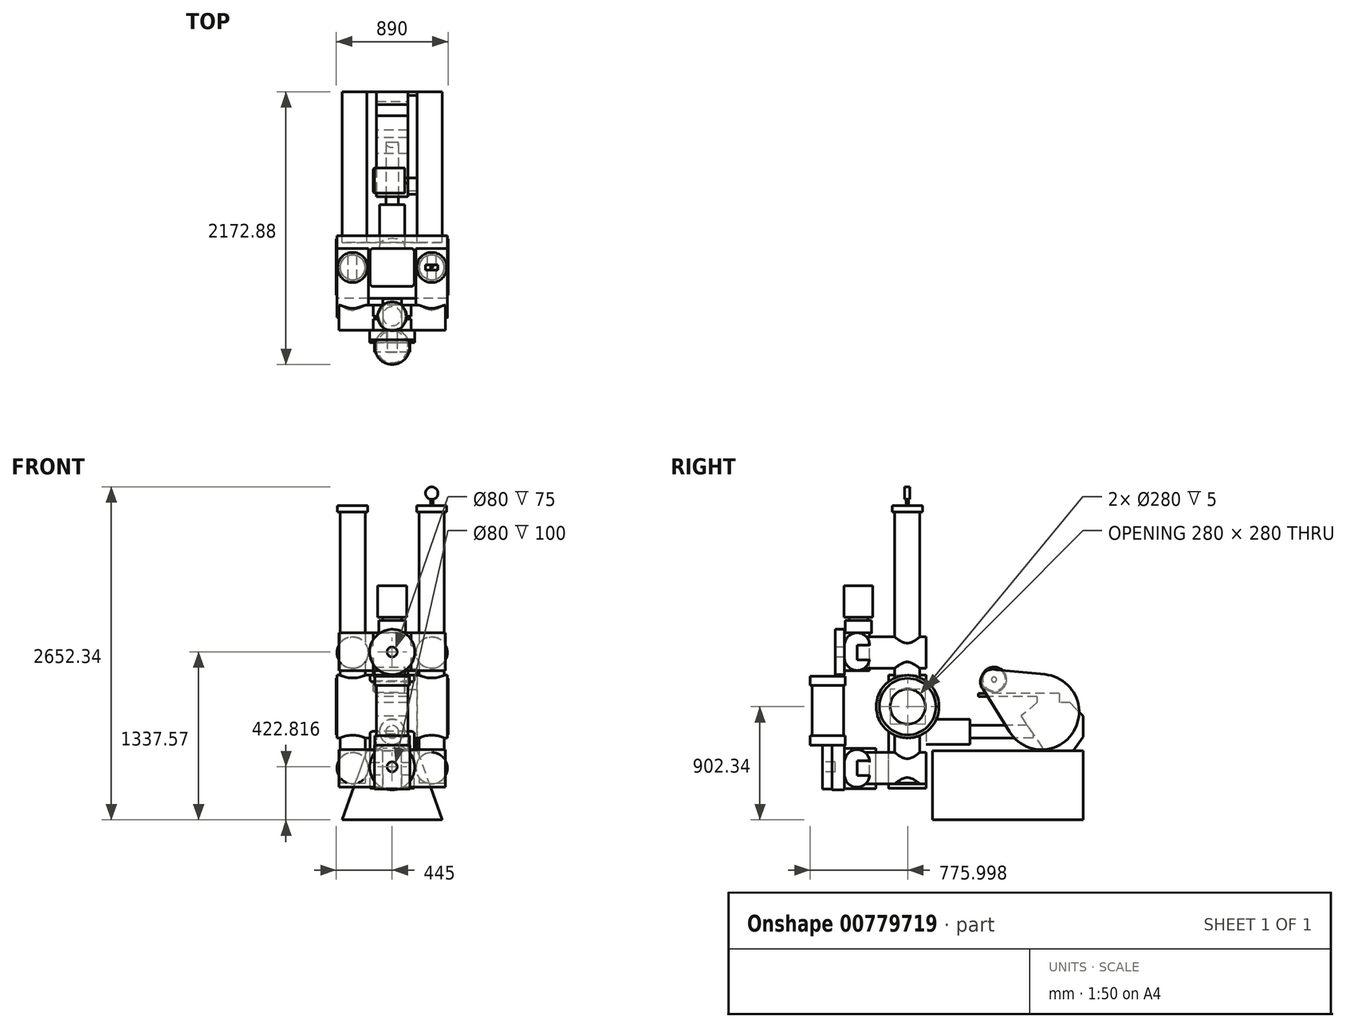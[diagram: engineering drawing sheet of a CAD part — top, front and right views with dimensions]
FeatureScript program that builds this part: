
annotation { "Feature Type Name" : "Feature", "Feature Type Description" : "" }
export const myFeature = defineFeature(function(context is Context, id is Id, definition is map)
    precondition{}
    {
        {
            var Q0;
            Q0=qCreatedBy(makeId("Front.planeOp"),FACE);
            var sketch = newSketch(context, id + "F0", { "sketchPlane" : qUnion([Q0])});
            skLineSegment(sketch, "E0", {"start": v(-400, 0) * mm, "end": v(-200, 550) * mm});
            skLineSegment(sketch, "E1", {"start": v(-200, 550) * mm, "end": v(200, 550) * mm});
            skLineSegment(sketch, "E2", {"start": v(200, 550) * mm, "end": v(400, 0) * mm});
            skLineSegment(sketch, "E3", {"start": v(400, 0) * mm, "end": v(-400, 0) * mm});
            skSolve(sketch);
        }
        {
            var Q0;
            Q0=makeQuery(id+"F0.imprint","IMPRINT",FACE,{"disambiguationData":[TD([[makeQuery(id+"F0.imprint","IMPRINT",EDGE,{"derivedFrom":sQuery(id+"F0.wireOp",EDGE,"E0")}),-1.0]])]});
            extrude(context, id + "F1", {"entities" : qUnion([Q0]), "depth" : 1200 * mm, "offsetDistance" : 25 * mm});
        }
        {
            var Q0;
            Q0=qCreatedBy(makeId("Right.planeOp"),FACE);
            var sketch = newSketch(context, id + "F2", { "sketchPlane" : qUnion([Q0])});
            skLineSegment(sketch, "E4", {"start": v(-84.81, 541.55) * mm, "end": v(0, 663.17) * mm});
            skLineSegment(sketch, "E5", {"start": v(0, 663.17) * mm, "end": v(0, 825.6) * mm});
            skLineSegment(sketch, "E6", {"start": v(0, 825.6) * mm, "end": v(-102.05, 933.54) * mm});
            skLineSegment(sketch, "E7", {"start": v(-102.05, 933.54) * mm, "end": v(-367.96, 933.54) * mm});
            skLineSegment(sketch, "E8", {"start": v(-367.96, 933.54) * mm, "end": v(-493.74, 825.6) * mm});
            skLineSegment(sketch, "E9", {"start": v(-493.74, 825.6) * mm, "end": v(-301.84, 542.34) * mm});
            skLineSegment(sketch, "E10", {"start": v(-301.84, 542.34) * mm, "end": v(-84.81, 541.55) * mm});
            skSolve(sketch);
        }
        {
            var Q0;
            Q0 = qSketchRegion(id + "F2", true);
            extrude(context, id + "F3", {"entities" : qUnion([Q0]), "operationType" : NewBodyOperationType.ADD, "endBound" : BoundingType.SYMMETRIC, "depth" : 250 * mm, "offsetDistance" : 25 * mm});
        }
        {
            var Q0;
            Q0=makeQuery(id+"F3.opExtrude","CAP_FACE",FACE,{"disambiguationData":[OSD([sQuery(id+"F2.wireOp",EDGE,"E4"),sQuery(id+"F2.wireOp",EDGE,"E5"),sQuery(id+"F2.wireOp",EDGE,"E6"),sQuery(id+"F2.wireOp",EDGE,"E7"),sQuery(id+"F2.wireOp",EDGE,"E8"),sQuery(id+"F2.wireOp",EDGE,"E9"),sQuery(id+"F2.wireOp",EDGE,"E10")])],"isStart":false});
            var sketch = newSketch(context, id + "F4", { "sketchPlane" : qUnion([Q0])});
            skArc(sketch, "E11", {"start": v(-586.28, 701.63) * mm, "mid": v(-76.54, 701.89) * mm, "end": v(-302.86, 1158.63) * mm});
            skArc(sketch, "E12", {"start": v(-688.12, 1195.57) * mm, "mid": v(-801.22, 1154.78) * mm, "end": v(-793.38, 1034.8) * mm});
            skLineSegment(sketch, "E13", {"start": v(-688.12, 1195.57) * mm, "end": v(-302.86, 1158.63) * mm});
            skLineSegment(sketch, "E14", {"start": v(-809.58, 1060.87) * mm, "end": v(-586.28, 701.63) * mm});
            skSolve(sketch);
        }
        {
            var Q0;
            Q0 = qSketchRegion(id + "F4", true);
            extrude(context, id + "F5", {"entities" : qUnion([Q0]), "operationType" : NewBodyOperationType.ADD, "depth" : 75 * mm, "offsetDistance" : 25 * mm});
        }
        {
            var Q0;
            Q0=makeQuery(id+"F3.opExtrude","SWEPT_FACE",FACE,{"disambiguationData":[OSD([sQuery(id+"F2.wireOp",EDGE,"E7")])]});
            var sketch = newSketch(context, id + "F6", { "sketchPlane" : qUnion([Q0])});
            skLineSegment(sketch, "E15.bottom", {"start": v(125, -190.52) * mm, "end": v(-125, -190.52) * mm});
            skLineSegment(sketch, "E15.top", {"start": v(125, -367.96) * mm, "end": v(-125, -367.96) * mm});
            skLineSegment(sketch, "E15.left", {"start": v(125, -190.52) * mm, "end": v(125, -367.96) * mm});
            skLineSegment(sketch, "E15.right", {"start": v(-125, -190.52) * mm, "end": v(-125, -367.96) * mm});
            skSolve(sketch);
        }
        {
            var Q0;
            Q0 = qSketchRegion(id + "F6", true);
            extrude(context, id + "F7", {"entities" : qUnion([Q0]), "operationType" : NewBodyOperationType.ADD, "depth" : 50 * mm, "offsetDistance" : 25 * mm});
        }
        {
            var Q0;
            Q0=makeQuery(id+"F7.opExtrude","CAP_FACE",FACE,{"disambiguationData":[OSD([sQuery(id+"F6.wireOp",EDGE,"E15.bottom"),sQuery(id+"F6.wireOp",EDGE,"E15.top"),sQuery(id+"F6.wireOp",EDGE,"E15.left"),sQuery(id+"F6.wireOp",EDGE,"E15.right")])],"isStart":false});
            var sketch = newSketch(context, id + "F8", { "sketchPlane" : qUnion([Q0])});
            skLineSegment(sketch, "E16.bottom", {"start": v(125, -190.52) * mm, "end": v(-125, -190.52) * mm});
            skLineSegment(sketch, "E16.top", {"start": v(125, -810.52) * mm, "end": v(-125, -810.52) * mm});
            skLineSegment(sketch, "E16.left", {"start": v(125, -190.52) * mm, "end": v(125, -810.52) * mm});
            skLineSegment(sketch, "E16.right", {"start": v(-125, -190.52) * mm, "end": v(-125, -810.52) * mm});
            skSolve(sketch);
        }
        {
            var Q0;
            Q0 = qSketchRegion(id + "F8", true);
            extrude(context, id + "F9", {"entities" : qUnion([Q0]), "operationType" : NewBodyOperationType.ADD, "depth" : 25 * mm, "offsetDistance" : 25 * mm});
        }
        {
            var Q0;
            {var subQ2=sQuery(id+"F4.wireOp",EDGE,"E14");var subQ3=sQuery(id+"F4.wireOp",EDGE,"E13");var subQ4=sQuery(id+"F4.wireOp",EDGE,"E12");var subQ6=sQuery(id+"F2.wireOp",EDGE,"E6");var subQ7=sQuery(id+"F4.wireOp",EDGE,"E11");Q0=makeQuery(id+"F9.boolean.opBoolean","SPLIT",FACE,{"disambiguationData":[TD([makeQuery(id+"F3.opExtrude","SWEPT_FACE",FACE,{"disambiguationData":[OSD([subQ6])]})])],"derivedFrom":makeQuery(id+"F5.opExtrude","CAP_FACE",FACE,{"disambiguationData":[OSD([subQ7,subQ4,subQ3,subQ2])],"isStart":true})});}
            var sketch = newSketch(context, id + "F10", { "sketchPlane" : qUnion([Q0])});
            skCircle(sketch, "E17", {"center": v(708.63, 1117.66) * mm, "radius": 20 * mm});
            skSolve(sketch);
        }
        {
            var Q0;
            Q0 = qSketchRegion(id + "F10", true);
            extrude(context, id + "F11", {"entities" : qUnion([Q0]), "operationType" : NewBodyOperationType.ADD, "depth" : 25 * mm, "offsetDistance" : 25 * mm});
        }
        {
            var Q0;
            Q0=makeQuery(id+"F11.opExtrude","CAP_FACE",FACE,{"disambiguationData":[OSD([sQuery(id+"F10.wireOp",EDGE,"E17")])],"isStart":false});
            var sketch = newSketch(context, id + "F12", { "sketchPlane" : qUnion([Q0])});
            skCircle(sketch, "E18", {"center": v(708.63, 1117.66) * mm, "radius": 100 * mm});
            skSolve(sketch);
        }
        {
            var Q0;
            Q0=makeQuery(id+"F12.imprint","IMPRINT",FACE,{"disambiguationData":[TD([[makeQuery(id+"F12.imprint","IMPRINT",EDGE,{"derivedFrom":sQuery(id+"F12.wireOp",EDGE,"E18")}),1.0]])]});
            var Q1;
            Q1=makeQuery(id+"F12.imprint","IMPRINT",FACE,{"disambiguationData":[TD([[makeQuery(id+"F12.imprint","IMPRINT",EDGE,{"derivedFrom":makeQuery(id+"F11.opExtrude","CAP_EDGE",EDGE,{"disambiguationData":[OSD([sQuery(id+"F10.wireOp",EDGE,"E17")])],"isStart":false})}),1.0]])]});
            extrude(context, id + "F13", {"entities" : qUnion([Q0, Q1]), "operationType" : NewBodyOperationType.ADD, "depth" : 250 * mm, "offsetDistance" : 25 * mm});
        }
        {
            var Q0;
            Q0=makeQuery(id+"F13.opExtrude","CAP_EDGE",EDGE,{"disambiguationData":[OSD([sQuery(id+"F12.wireOp",EDGE,"E18")])],"isStart":false});
            chamfer(context, id + "F14", {"entities" : qUnion([Q0]), "width" : 10 * mm, "tangentPropagation" : true});
        }
        {
            var Q0;
            Q0=makeQuery(id+"F9.opExtrude","SWEPT_FACE",FACE,{"disambiguationData":[OSD([sQuery(id+"F8.wireOp",EDGE,"E16.top")])]});
            extrude(context, id + "F15", {"entities" : qUnion([Q0]), "operationType" : NewBodyOperationType.ADD, "depth" : 25 * mm, "offsetDistance" : 25 * mm});
        }
        {
            var Q0;
            Q0=makeQuery(id+"F1.opExtrude","CAP_FACE",FACE,{"disambiguationData":[OSD([sQuery(id+"F0.wireOp",EDGE,"E0"),sQuery(id+"F0.wireOp",EDGE,"E1"),sQuery(id+"F0.wireOp",EDGE,"E2"),sQuery(id+"F0.wireOp",EDGE,"E3")])],"isStart":false});
            var sketch = newSketch(context, id + "F16", { "sketchPlane" : qUnion([Q0])});
            skCircle(sketch, "E19", {"center": v(0, 702.34) * mm, "radius": 50 * mm});
            skSolve(sketch);
        }
        {
            var Q0;
            Q0=makeQuery(id+"F16.imprint","IMPRINT",FACE,{"disambiguationData":[TD([[makeQuery(id+"F16.imprint","IMPRINT",EDGE,{"derivedFrom":sQuery(id+"F16.wireOp",EDGE,"E19")}),1.0]])]});
            extrude(context, id + "F17", {"entities" : qUnion([Q0]), "operationType" : NewBodyOperationType.ADD, "oppositeDirection" : true, "depth" : 800 * mm, "offsetDistance" : 25 * mm});
        }
        {
            var Q0;
            Q0=makeQuery(id+"F17.opExtrude","CAP_FACE",FACE,{"disambiguationData":[OSD([sQuery(id+"F16.wireOp",EDGE,"E19")])],"isStart":true});
            var sketch = newSketch(context, id + "F18", { "sketchPlane" : qUnion([Q0])});
            skCircle(sketch, "E20", {"center": v(0, 702.34) * mm, "radius": 100 * mm});
            skSolve(sketch);
        }
        {
            var Q0;
            Q0=makeQuery(id+"F18.imprint","IMPRINT",FACE,{"disambiguationData":[TD([[makeQuery(id+"F18.imprint","IMPRINT",EDGE,{"derivedFrom":makeQuery(id+"F17.opExtrude","CAP_EDGE",EDGE,{"disambiguationData":[OSD([sQuery(id+"F16.wireOp",EDGE,"E19")])],"isStart":true})}),1.0]])]});
            var Q1;
            Q1=makeQuery(id+"F18.imprint","IMPRINT",FACE,{"disambiguationData":[TD([[makeQuery(id+"F18.imprint","IMPRINT",EDGE,{"derivedFrom":sQuery(id+"F18.wireOp",EDGE,"E20")}),1.0]])]});
            extrude(context, id + "F19", {"entities" : qUnion([Q0, Q1]), "operationType" : NewBodyOperationType.ADD, "oppositeDirection" : true, "depth" : 300 * mm, "offsetDistance" : 25 * mm, "hasSecondDirection" : true, "secondDirectionOppositeDirection" : false, "secondDirectionDepth" : 200 * mm});
        }
        {
            var Q0;
            Q0=makeQuery(id+"F19.opExtrude","CAP_FACE",FACE,{"disambiguationData":[OSD([sQuery(id+"F18.wireOp",EDGE,"E20")])],"isStart":true});
            var sketch = newSketch(context, id + "F20", { "sketchPlane" : qUnion([Q0])});
            skLineSegment(sketch, "E21.bottom", {"start": v(175, 252.34) * mm, "end": v(-175, 252.34) * mm});
            skLineSegment(sketch, "E21.top", {"start": v(175, 1152.34) * mm, "end": v(-175, 1152.34) * mm});
            skLineSegment(sketch, "E21.left", {"start": v(175, 252.34) * mm, "end": v(175, 1152.34) * mm});
            skLineSegment(sketch, "E21.right", {"start": v(-175, 252.34) * mm, "end": v(-175, 1152.34) * mm});
            skPoint(sketch, "E21.middle", {"position": v(0, 702.34) * mm});
            skSolve(sketch);
        }
        {
            var Q0;
            Q0 = qSketchRegion(id + "F20", true);
            extrude(context, id + "F21", {"entities" : qUnion([Q0]), "operationType" : NewBodyOperationType.ADD, "endBound" : BoundingType.SYMMETRIC, "depth" : 300 * mm, "offsetDistance" : 25 * mm});
        }
        {
            var Q0;
            Q0=makeQuery(id+"F21.opExtrude","CAP_EDGE",EDGE,{"disambiguationData":[OSD([sQuery(id+"F20.wireOp",EDGE,"E21.right")])],"isStart":false});
            var Q1;
            Q1=makeQuery(id+"F21.opExtrude","CAP_EDGE",EDGE,{"disambiguationData":[OSD([sQuery(id+"F20.wireOp",EDGE,"E21.left")])],"isStart":false});
            var Q2;
            Q2=makeQuery(id+"F21.opExtrude","CAP_EDGE",EDGE,{"disambiguationData":[OSD([sQuery(id+"F20.wireOp",EDGE,"E21.left")])],"isStart":true});
            var Q3;
            Q3=makeQuery(id+"F21.opExtrude","CAP_EDGE",EDGE,{"disambiguationData":[OSD([sQuery(id+"F20.wireOp",EDGE,"E21.right")])],"isStart":true});
            fillet(context, id + "F22", {"entities" : qUnion([Q0, Q1, Q2, Q3]), "radius" : 20 * mm, "tangentPropagation" : true, "allowEdgeOverflow" : false});
        }
        {
            var Q0;
            Q0=qCreatedBy(makeId("Right.planeOp"),FACE);
            var sketch = newSketch(context, id + "F23", { "sketchPlane" : qUnion([Q0])});
            skCircle(sketch, "E22", {"center": v(-1396.88, 902.34) * mm, "radius": 250 * mm});
            skSolve(sketch);
        }
        {
            var Q0;
            Q0=makeQuery(id+"F23.imprint","IMPRINT",FACE,{"disambiguationData":[TD([[makeQuery(id+"F23.imprint","IMPRINT",EDGE,{"derivedFrom":sQuery(id+"F23.wireOp",EDGE,"E22")}),1.0]])]});
            extrude(context, id + "F24", {"entities" : qUnion([Q0]), "operationType" : NewBodyOperationType.ADD, "endBound" : BoundingType.SYMMETRIC, "depth" : 880 * mm, "offsetDistance" : 25 * mm});
        }
        {
            var Q0;
            Q0=makeQuery(id+"F21.opExtrude","SWEPT_FACE",FACE,{"disambiguationData":[OSD([sQuery(id+"F20.wireOp",EDGE,"E21.top")])]});
            var sketch = newSketch(context, id + "F25", { "sketchPlane" : qUnion([Q0])});
            skCircle(sketch, "E23", {"center": v(-315, -1400) * mm, "radius": 100 * mm});
            skCircle(sketch, "E24.MirrorC", {"center": v(315, -1400) * mm, "radius": 100 * mm});
            skSolve(sketch);
        }
        {
            var Q0;
            Q0 = qSketchRegion(id + "F25", true);
            extrude(context, id + "F26", {"entities" : qUnion([Q0]), "operationType" : NewBodyOperationType.ADD, "depth" : 1300 * mm, "offsetDistance" : 25 * mm, "hasSecondDirection" : true, "secondDirectionOppositeDirection" : true, "secondDirectionDepth" : 860 * mm});
        }
        {
            var Q0;
            {var subQ0=sQuery(id+"F20.wireOp",EDGE,"E21.right");var subQ1=sQuery(id+"F20.wireOp",EDGE,"E21.left");var subQ2=sQuery(id+"F20.wireOp",EDGE,"E21.bottom");Q0=makeQuery(id+"F24.boolean.opBoolean","SPLIT",FACE,{"disambiguationData":[TD([makeQuery(id+"F19.opExtrude","SWEPT_FACE",FACE,{"disambiguationData":[OSD([sQuery(id+"F18.wireOp",EDGE,"E20")])]})])],"derivedFrom":makeQuery(id+"F21.opExtrude","CAP_FACE",FACE,{"disambiguationData":[OSD([subQ2,sQuery(id+"F20.wireOp",EDGE,"E21.top"),subQ1,subQ0])],"isStart":true})});}
            var sketch = newSketch(context, id + "F27", { "sketchPlane" : qUnion([Q0])});
            skCircle(sketch, "E25", {"center": v(315, 412.34) * mm, "radius": 125 * mm});
            skCircle(sketch, "E26.MirrorC", {"center": v(-315, 412.34) * mm, "radius": 125 * mm});
            skCircle(sketch, "E27.0.1.0", {"center": v(315, 1332.34) * mm, "radius": 125 * mm});
            skCircle(sketch, "E27.0.1.1", {"center": v(-315, 1332.34) * mm, "radius": 125 * mm});
            skLineSegment(sketch, "E27.direction1", {"start": v(315, 412.34) * mm, "end": v(340, 412.34) * mm, "construction": true});
            skLineSegment(sketch, "E27.direction2", {"start": v(315, 412.34) * mm, "end": v(315, 1332.34) * mm, "construction": true});
            skSolve(sketch);
        }
        {
            var Q0;
            Q0 = qSketchRegion(id + "F27", true);
            extrude(context, id + "F28", {"entities" : qUnion([Q0]), "operationType" : NewBodyOperationType.ADD, "oppositeDirection" : true, "depth" : 550 * mm, "offsetDistance" : 25 * mm});
        }
        {
            var Q0;
            Q0=makeQuery(id+"F28.opExtrude","CAP_FACE",FACE,{"disambiguationData":[OSD([sQuery(id+"F27.wireOp",EDGE,"E25")])],"isStart":false});
            var sketch = newSketch(context, id + "F29", { "sketchPlane" : qUnion([Q0])});
            skLineSegment(sketch, "E28.bottom", {"start": v(-425, 560) * mm, "end": v(425, 560) * mm});
            skLineSegment(sketch, "E28.top", {"start": v(-425, 260) * mm, "end": v(425, 260) * mm});
            skLineSegment(sketch, "E28.left", {"start": v(-425, 560) * mm, "end": v(-425, 260) * mm});
            skLineSegment(sketch, "E28.right", {"start": v(425, 560) * mm, "end": v(425, 260) * mm});
            skLineSegment(sketch, "E29.0.1.0", {"start": v(-425, 1490) * mm, "end": v(-425, 1190) * mm});
            skLineSegment(sketch, "E29.0.1.1", {"start": v(-425, 1190) * mm, "end": v(425, 1190) * mm});
            skLineSegment(sketch, "E29.0.1.2", {"start": v(-425, 1490) * mm, "end": v(425, 1490) * mm});
            skLineSegment(sketch, "E29.0.1.3", {"start": v(425, 1490) * mm, "end": v(425, 1190) * mm});
            skLineSegment(sketch, "E29.direction1", {"start": v(-425, 260) * mm, "end": v(-400, 260) * mm, "construction": true});
            skLineSegment(sketch, "E29.direction2", {"start": v(-425, 260) * mm, "end": v(-425, 1190) * mm, "construction": true});
            skSolve(sketch);
        }
        {
            var Q0;
            Q0 = qSketchRegion(id + "F29", true);
            extrude(context, id + "F30", {"entities" : qUnion([Q0]), "operationType" : NewBodyOperationType.ADD, "endBound" : BoundingType.SYMMETRIC, "depth" : 200 * mm, "offsetDistance" : 25 * mm});
        }
        {
            var Q0;
            Q0=makeQuery(id+"F30.opExtrude","CAP_EDGE",EDGE,{"disambiguationData":[OSD([sQuery(id+"F29.wireOp",EDGE,"E28.bottom")])],"isStart":false});
            var Q1;
            Q1=makeQuery(id+"F30.opExtrude","CAP_EDGE",EDGE,{"disambiguationData":[OSD([sQuery(id+"F29.wireOp",EDGE,"E28.top")])],"isStart":false});
            var Q2;
            Q2=makeQuery(id+"F30.opExtrude","CAP_EDGE",EDGE,{"disambiguationData":[OSD([sQuery(id+"F29.wireOp",EDGE,"E28.top")])],"isStart":true});
            var Q3;
            Q3=makeQuery(id+"F30.opExtrude","CAP_EDGE",EDGE,{"disambiguationData":[OSD([sQuery(id+"F29.wireOp",EDGE,"E28.bottom")])],"isStart":true});
            fillet(context, id + "F31", {"entities" : qUnion([Q0, Q1, Q2, Q3]), "radius" : 100 * mm, "tangentPropagation" : true, "allowEdgeOverflow" : false});
        }
        {
            var Q0;
            Q0=makeQuery(id+"F30.opExtrude","CAP_EDGE",EDGE,{"disambiguationData":[OSD([sQuery(id+"F29.wireOp",EDGE,"E29.0.1.2")])],"isStart":false});
            var Q1;
            Q1=makeQuery(id+"F30.opExtrude","CAP_EDGE",EDGE,{"disambiguationData":[OSD([sQuery(id+"F29.wireOp",EDGE,"E29.0.1.2")])],"isStart":true});
            var Q2;
            Q2=makeQuery(id+"F30.opExtrude","CAP_EDGE",EDGE,{"disambiguationData":[OSD([sQuery(id+"F29.wireOp",EDGE,"E29.0.1.1")])],"isStart":false});
            var Q3;
            Q3=makeQuery(id+"F30.opExtrude","CAP_EDGE",EDGE,{"disambiguationData":[OSD([sQuery(id+"F29.wireOp",EDGE,"E29.0.1.1")])],"isStart":true});
            fillet(context, id + "F32", {"entities" : qUnion([Q0, Q1, Q2, Q3]), "radius" : 100 * mm, "tangentPropagation" : true, "allowEdgeOverflow" : false});
        }
        {
            var Q0;
            Q0=makeQuery(id+"F30.opExtrude","CAP_FACE",FACE,{"disambiguationData":[OSD([sQuery(id+"F29.wireOp",EDGE,"E28.bottom"),sQuery(id+"F29.wireOp",EDGE,"E28.top"),sQuery(id+"F29.wireOp",EDGE,"E28.left"),sQuery(id+"F29.wireOp",EDGE,"E28.right")])],"isStart":false});
            var sketch = newSketch(context, id + "F33", { "sketchPlane" : qUnion([Q0])});
            skLineSegment(sketch, "E30.bottom", {"start": v(75, 250) * mm, "end": v(-75, 250) * mm});
            skLineSegment(sketch, "E30.top", {"start": v(75, 570) * mm, "end": v(-75, 570) * mm});
            skLineSegment(sketch, "E30.left", {"start": v(75, 250) * mm, "end": v(75, 570) * mm});
            skLineSegment(sketch, "E30.right", {"start": v(-75, 250) * mm, "end": v(-75, 570) * mm});
            skPoint(sketch, "E30.middle", {"position": v(0, 410) * mm});
            skSolve(sketch);
        }
        {
            var Q0;
            Q0 = qSketchRegion(id + "F33", true);
            extrude(context, id + "F34", {"entities" : qUnion([Q0]), "operationType" : NewBodyOperationType.ADD, "oppositeDirection" : true, "depth" : 250 * mm, "offsetDistance" : 25 * mm});
        }
        {
            var Q0;
            Q0=makeQuery(id+"F34.boolean.opBoolean","MERGE",FACE,{"derivedFrom":[makeQuery(id+"F30.opExtrude","CAP_FACE",FACE,{"disambiguationData":[OSD([sQuery(id+"F29.wireOp",EDGE,"E28.bottom"),sQuery(id+"F29.wireOp",EDGE,"E28.top"),sQuery(id+"F29.wireOp",EDGE,"E28.left"),sQuery(id+"F29.wireOp",EDGE,"E28.right")])],"isStart":false}),makeQuery(id+"F34.opExtrude","CAP_FACE",FACE,{"disambiguationData":[OSD([sQuery(id+"F33.wireOp",EDGE,"E30.bottom"),sQuery(id+"F33.wireOp",EDGE,"E30.top"),sQuery(id+"F33.wireOp",EDGE,"E30.left"),sQuery(id+"F33.wireOp",EDGE,"E30.right")])],"isStart":true})]});
            var sketch = newSketch(context, id + "F35", { "sketchPlane" : qUnion([Q0])});
            skCircle(sketch, "E31", {"center": v(0, 420) * mm, "radius": 180 * mm});
            skSolve(sketch);
        }
        {
            var Q0;
            Q0 = qSketchRegion(id + "F35", true);
            extrude(context, id + "F36", {"entities" : qUnion([Q0]), "operationType" : NewBodyOperationType.ADD, "depth" : 100 * mm, "offsetDistance" : 25 * mm});
        }
        {
            var Q0;
            Q0=makeQuery(id+"F36.opExtrude","CAP_FACE",FACE,{"disambiguationData":[OSD([sQuery(id+"F35.wireOp",EDGE,"E31")])],"isStart":false});
            var sketch = newSketch(context, id + "F37", { "sketchPlane" : qUnion([Q0])});
            skLineSegment(sketch, "E32.bottom", {"start": v(140, 245) * mm, "end": v(-140, 245) * mm});
            skLineSegment(sketch, "E32.top", {"start": v(140, 595) * mm, "end": v(-140, 595) * mm});
            skLineSegment(sketch, "E32.left", {"start": v(140, 245) * mm, "end": v(140, 595) * mm});
            skLineSegment(sketch, "E32.right", {"start": v(-140, 245) * mm, "end": v(-140, 595) * mm});
            skPoint(sketch, "E32.middle", {"position": v(0, 420) * mm});
            skSolve(sketch);
        }
        {
            var Q0;
            Q0 = qSketchRegion(id + "F37", true);
            extrude(context, id + "F38", {"entities" : qUnion([Q0]), "operationType" : NewBodyOperationType.ADD, "depth" : 75 * mm, "offsetDistance" : 25 * mm});
        }
        {
            var Q0;
            Q0=makeQuery(id+"F38.opExtrude","SWEPT_FACE",FACE,{"disambiguationData":[OSD([sQuery(id+"F37.wireOp",EDGE,"E32.top")])]});
            var sketch = newSketch(context, id + "F39", { "sketchPlane" : qUnion([Q0])});
            skCircle(sketch, "E33", {"center": v(0, -2033.26) * mm, "radius": 139.62 * mm});
            skSolve(sketch);
        }
        {
            var Q0;
            Q0 = qSketchRegion(id + "F39", true);
            extrude(context, id + "F40", {"entities" : qUnion([Q0]), "operationType" : NewBodyOperationType.ADD, "depth" : 75 * mm, "offsetDistance" : 25 * mm});
        }
        {
            var Q0;
            Q0=makeQuery(id+"F40.opExtrude","CAP_FACE",FACE,{"disambiguationData":[OSD([sQuery(id+"F39.wireOp",EDGE,"E33")])],"isStart":false});
            var sketch = newSketch(context, id + "F41", { "sketchPlane" : qUnion([Q0])});
            skCircle(sketch, "E34", {"center": v(0, -2033.26) * mm, "radius": 125 * mm});
            skSolve(sketch);
        }
        {
            var Q0;
            Q0=makeQuery(id+"F41.imprint","IMPRINT",FACE,{"disambiguationData":[TD([[makeQuery(id+"F41.imprint","IMPRINT",EDGE,{"derivedFrom":sQuery(id+"F41.wireOp",EDGE,"E34")}),1.0]])]});
            extrude(context, id + "F42", {"entities" : qUnion([Q0]), "operationType" : NewBodyOperationType.ADD, "depth" : 400 * mm, "offsetDistance" : 25 * mm});
        }
        {
            var Q0;
            Q0=makeQuery(id+"F42.opExtrude","CAP_FACE",FACE,{"disambiguationData":[OSD([sQuery(id+"F41.wireOp",EDGE,"E34")])],"isStart":false});
            var sketch = newSketch(context, id + "F43", { "sketchPlane" : qUnion([Q0])});
            skCircle(sketch, "E35.0", {"center": v(0, -2033.26) * mm, "radius": 139.62 * mm});
            skSolve(sketch);
        }
        {
            var Q0;
            Q0 = qSketchRegion(id + "F43", true);
            extrude(context, id + "F44", {"entities" : qUnion([Q0]), "operationType" : NewBodyOperationType.ADD, "depth" : 75 * mm, "offsetDistance" : 25 * mm});
        }
        {
            var Q0;
            Q0=makeQuery(id+"F30.opExtrude","CAP_FACE",FACE,{"disambiguationData":[OSD([sQuery(id+"F29.wireOp",EDGE,"E29.0.1.0"),sQuery(id+"F29.wireOp",EDGE,"E29.0.1.1"),sQuery(id+"F29.wireOp",EDGE,"E29.0.1.2"),sQuery(id+"F29.wireOp",EDGE,"E29.0.1.3")])],"isStart":false});
            var sketch = newSketch(context, id + "F45", { "sketchPlane" : qUnion([Q0])});
            skLineSegment(sketch, "E36.bottom", {"start": v(150, 1189.4) * mm, "end": v(-150, 1189.4) * mm});
            skLineSegment(sketch, "E36.top", {"start": v(150, 1489.4) * mm, "end": v(-150, 1489.4) * mm});
            skLineSegment(sketch, "E36.left", {"start": v(150, 1189.4) * mm, "end": v(150, 1489.4) * mm});
            skLineSegment(sketch, "E36.right", {"start": v(-150, 1189.4) * mm, "end": v(-150, 1489.4) * mm});
            skPoint(sketch, "E36.middle", {"position": v(0, 1339.4) * mm});
            skSolve(sketch);
        }
        {
            var Q0;
            Q0 = qSketchRegion(id + "F45", true);
            extrude(context, id + "F46", {"entities" : qUnion([Q0]), "operationType" : NewBodyOperationType.ADD, "oppositeDirection" : true, "depth" : 200 * mm, "offsetDistance" : 25 * mm});
        }
        {
            var Q0;
            Q0=makeQuery(id+"F46.boolean.opBoolean","MERGE",FACE,{"derivedFrom":[makeQuery(id+"F30.opExtrude","CAP_FACE",FACE,{"disambiguationData":[OSD([sQuery(id+"F29.wireOp",EDGE,"E29.0.1.0"),sQuery(id+"F29.wireOp",EDGE,"E29.0.1.1"),sQuery(id+"F29.wireOp",EDGE,"E29.0.1.2"),sQuery(id+"F29.wireOp",EDGE,"E29.0.1.3")])],"isStart":false}),makeQuery(id+"F46.opExtrude","CAP_FACE",FACE,{"disambiguationData":[OSD([sQuery(id+"F45.wireOp",EDGE,"E36.bottom"),sQuery(id+"F45.wireOp",EDGE,"E36.top"),sQuery(id+"F45.wireOp",EDGE,"E36.left"),sQuery(id+"F45.wireOp",EDGE,"E36.right")])],"isStart":true})]});
            var sketch = newSketch(context, id + "F47", { "sketchPlane" : qUnion([Q0])});
            skCircle(sketch, "E37", {"center": v(0, 1337.57) * mm, "radius": 180 * mm});
            skSolve(sketch);
        }
        {
            var Q0;
            Q0 = qSketchRegion(id + "F47", true);
            extrude(context, id + "F48", {"entities" : qUnion([Q0]), "operationType" : NewBodyOperationType.ADD, "depth" : 75 * mm, "offsetDistance" : 25 * mm});
        }
        {
            var Q0;
            Q0=makeQuery(id+"F48.opExtrude","CAP_FACE",FACE,{"disambiguationData":[OSD([sQuery(id+"F47.wireOp",EDGE,"E37")])],"isStart":false});
            var sketch = newSketch(context, id + "F49", { "sketchPlane" : qUnion([Q0])});
            skCircle(sketch, "E38", {"center": v(0, 1337.57) * mm, "radius": 40 * mm});
            skSolve(sketch);
        }
        {
            var Q0;
            Q0=makeQuery(id+"F49.imprint","IMPRINT",FACE,{"disambiguationData":[TD([[makeQuery(id+"F49.imprint","IMPRINT",EDGE,{"derivedFrom":sQuery(id+"F49.wireOp",EDGE,"E38")}),1.0]])]});
            extrude(context, id + "F50", {"entities" : qUnion([Q0]), "operationType" : NewBodyOperationType.REMOVE, "oppositeDirection" : true, "depth" : 75 * mm, "offsetDistance" : 25 * mm});
        }
        {
            var Q0;
            Q0=makeQuery(id+"F38.opExtrude","CAP_FACE",FACE,{"disambiguationData":[OSD([sQuery(id+"F37.wireOp",EDGE,"E32.bottom"),sQuery(id+"F37.wireOp",EDGE,"E32.top"),sQuery(id+"F37.wireOp",EDGE,"E32.left"),sQuery(id+"F37.wireOp",EDGE,"E32.right")])],"isStart":false});
            var sketch = newSketch(context, id + "F51", { "sketchPlane" : qUnion([Q0])});
            skCircle(sketch, "E39", {"center": v(0, 422.82) * mm, "radius": 40 * mm});
            skSolve(sketch);
        }
        {
            var Q0;
            Q0 = qSketchRegion(id + "F51", true);
            extrude(context, id + "F52", {"entities" : qUnion([Q0]), "operationType" : NewBodyOperationType.REMOVE, "oppositeDirection" : true, "depth" : 100 * mm, "offsetDistance" : 25 * mm});
        }
        {
            var Q0;
            {var subQ1=sQuery(id+"F29.wireOp",EDGE,"E29.0.1.2");var subQ3=sQuery(id+"F45.wireOp",EDGE,"E36.top");Q0=makeQuery(id+"F46.boolean.opBoolean","SPLIT",FACE,{"disambiguationData":[TD([makeQuery(id+"F30.opExtrude","CAP_FACE",FACE,{"disambiguationData":[OSD([sQuery(id+"F29.wireOp",EDGE,"E29.0.1.0"),sQuery(id+"F29.wireOp",EDGE,"E29.0.1.1"),subQ1,sQuery(id+"F29.wireOp",EDGE,"E29.0.1.3")])],"isStart":true})])],"derivedFrom":makeQuery(id+"F46.opExtrude","SWEPT_FACE",FACE,{"disambiguationData":[OSD([subQ3])]})});}
            var sketch = newSketch(context, id + "F53", { "sketchPlane" : qUnion([Q0])});
            skCircle(sketch, "E40", {"center": v(0, -1788.98) * mm, "radius": 105 * mm});
            skSolve(sketch);
        }
        {
            var Q0;
            Q0 = qSketchRegion(id + "F53", true);
            extrude(context, id + "F54", {"entities" : qUnion([Q0]), "operationType" : NewBodyOperationType.ADD, "depth" : 100 * mm, "offsetDistance" : 25 * mm});
        }
        {
            var Q0;
            Q0=makeQuery(id+"F54.opExtrude","CAP_FACE",FACE,{"disambiguationData":[OSD([sQuery(id+"F53.wireOp",EDGE,"E40")])],"isStart":false});
            var sketch = newSketch(context, id + "F55", { "sketchPlane" : qUnion([Q0])});
            skCircle(sketch, "E41", {"center": v(0, -1788.98) * mm, "radius": 75 * mm});
            skSolve(sketch);
        }
        {
            var Q0;
            Q0=makeQuery(id+"F55.imprint","IMPRINT",FACE,{"disambiguationData":[TD([[makeQuery(id+"F55.imprint","IMPRINT",EDGE,{"derivedFrom":sQuery(id+"F55.wireOp",EDGE,"E41")}),1.0]])]});
            extrude(context, id + "F56", {"entities" : qUnion([Q0]), "operationType" : NewBodyOperationType.ADD, "depth" : 25 * mm, "offsetDistance" : 25 * mm});
        }
        {
            var Q0;
            Q0=makeQuery(id+"F56.opExtrude","CAP_FACE",FACE,{"disambiguationData":[OSD([sQuery(id+"F55.wireOp",EDGE,"E41")])],"isStart":false});
            var sketch = newSketch(context, id + "F57", { "sketchPlane" : qUnion([Q0])});
            skCircle(sketch, "E42", {"center": v(0, -1788.98) * mm, "radius": 115 * mm});
            skSolve(sketch);
        }
        {
            var Q0;
            Q0 = qSketchRegion(id + "F57", true);
            extrude(context, id + "F58", {"entities" : qUnion([Q0]), "operationType" : NewBodyOperationType.ADD, "depth" : 250 * mm, "offsetDistance" : 25 * mm});
        }
        {
            var Q0;
            Q0=makeQuery(id+"F24.opExtrude","CAP_FACE",FACE,{"disambiguationData":[OSD([sQuery(id+"F23.wireOp",EDGE,"E22")])],"isStart":true});
            var sketch = newSketch(context, id + "F59", { "sketchPlane" : qUnion([Q0])});
            skCircle(sketch, "E43", {"center": v(1396.88, 902.34) * mm, "radius": 140 * mm});
            skCircle(sketch, "E44", {"center": v(1396.88, 902.34) * mm, "radius": 225 * mm});
            skSolve(sketch);
        }
        {
            var Q0;
            Q0=makeQuery(id+"F59.imprint","IMPRINT",FACE,{"disambiguationData":[TD([[makeQuery(id+"F59.imprint","IMPRINT",EDGE,{"derivedFrom":sQuery(id+"F59.wireOp",EDGE,"E43")}),-1.0]])]});
            extrude(context, id + "F60", {"entities" : qUnion([Q0]), "operationType" : NewBodyOperationType.ADD, "depth" : 5 * mm, "offsetDistance" : 25 * mm, "hasSecondDirection" : true, "secondDirectionOppositeDirection" : true, "secondDirectionDepth" : 885 * mm});
        }
        {
            var Q0;
            Q0=makeQuery(id+"F26.opExtrude","CAP_FACE",FACE,{"disambiguationData":[OSD([sQuery(id+"F25.wireOp",EDGE,"E23")])],"isStart":false});
            var sketch = newSketch(context, id + "F61", { "sketchPlane" : qUnion([Q0])});
            skCircle(sketch, "E45", {"center": v(-315, -1400) * mm, "radius": 120 * mm});
            skCircle(sketch, "E46.MirrorC", {"center": v(315, -1400) * mm, "radius": 120 * mm});
            skSolve(sketch);
        }
        {
            var Q0;
            Q0 = qSketchRegion(id + "F61", true);
            extrude(context, id + "F62", {"entities" : qUnion([Q0]), "operationType" : NewBodyOperationType.ADD, "depth" : 50 * mm, "offsetDistance" : 25 * mm});
        }
        {
            var Q0;
            Q0=makeQuery(id+"F62.opExtrude","CAP_FACE",FACE,{"disambiguationData":[OSD([sQuery(id+"F61.wireOp",EDGE,"E46.MirrorC")])],"isStart":false});
            var sketch = newSketch(context, id + "F63", { "sketchPlane" : qUnion([Q0])});
            skCircle(sketch, "E47", {"center": v(315, -1400) * mm, "radius": 10 * mm});
            skSolve(sketch);
        }
        {
            var Q0;
            Q0=makeQuery(id+"F63.imprint","IMPRINT",FACE,{"disambiguationData":[TD([[makeQuery(id+"F63.imprint","IMPRINT",EDGE,{"derivedFrom":sQuery(id+"F63.wireOp",EDGE,"E47")}),1.0]])]});
            extrude(context, id + "F64", {"entities" : qUnion([Q0]), "operationType" : NewBodyOperationType.ADD, "depth" : 100 * mm, "offsetDistance" : 25 * mm});
        }
        {
            var Q0;
            Q0=makeQuery(id+"F64.opExtrude","CAP_FACE",FACE,{"disambiguationData":[OSD([sQuery(id+"F63.wireOp",EDGE,"E47")])],"isStart":false});
            var sketch = newSketch(context, id + "F65", { "sketchPlane" : qUnion([Q0])});
            skLineSegment(sketch, "E48.bottom", {"start": v(265, -1380) * mm, "end": v(365, -1380) * mm});
            skLineSegment(sketch, "E48.top", {"start": v(265, -1420) * mm, "end": v(365, -1420) * mm});
            skLineSegment(sketch, "E48.left", {"start": v(265, -1380) * mm, "end": v(265, -1420) * mm});
            skLineSegment(sketch, "E48.right", {"start": v(365, -1380) * mm, "end": v(365, -1420) * mm});
            skPoint(sketch, "E48.middle", {"position": v(315, -1400) * mm});
            skSolve(sketch);
        }
        {
            var Q0;
            Q0 = qSketchRegion(id + "F65", true);
            extrude(context, id + "F66", {"entities" : qUnion([Q0]), "operationType" : NewBodyOperationType.ADD, "endBound" : BoundingType.SYMMETRIC, "depth" : 100 * mm, "offsetDistance" : 25 * mm});
        }
        {
            var Q0;
            Q0=makeQuery(id+"F66.opExtrude","CAP_EDGE",EDGE,{"disambiguationData":[OSD([sQuery(id+"F65.wireOp",EDGE,"E48.right")])],"isStart":false});
            var Q1;
            Q1=makeQuery(id+"F66.opExtrude","CAP_EDGE",EDGE,{"disambiguationData":[OSD([sQuery(id+"F65.wireOp",EDGE,"E48.left")])],"isStart":false});
            var Q2;
            Q2=makeQuery(id+"F66.opExtrude","CAP_EDGE",EDGE,{"disambiguationData":[OSD([sQuery(id+"F65.wireOp",EDGE,"E48.left")])],"isStart":true});
            var Q3;
            Q3=makeQuery(id+"F66.opExtrude","CAP_EDGE",EDGE,{"disambiguationData":[OSD([sQuery(id+"F65.wireOp",EDGE,"E48.right")])],"isStart":true});
            fillet(context, id + "F67", {"entities" : qUnion([Q0, Q1, Q2, Q3]), "radius" : 50 * mm, "tangentPropagation" : true, "allowEdgeOverflow" : false});
        }
    });
